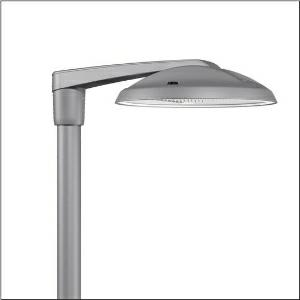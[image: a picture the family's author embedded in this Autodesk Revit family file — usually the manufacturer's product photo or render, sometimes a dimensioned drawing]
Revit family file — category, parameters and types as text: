
# Revit family: dl_r__50_iq_mini___st1_0a_5xa248d31v08le_d4cd
name_source: partatom
category: Lighting Fixtures
units: mm (PartAtom-declared; Revit-internal decimal feet)

## family parameters
Cut with Voids When Loaded = No
Host = Face
Light Source = No
Part Type = Normal
Room Calculation Point = No
Round Connector Dimension = Use Diameter
Shared = No

## types (1)
- --- (1 x LED, 10390 lm, 66 W, 3000K)
    Apparent Load = 66 VA
    CIE Flux Codes = 37 72 97 100 100
    Color Rendering = 70
    Color Temperature = 3000K
    Default Elevation = 1800 mm
    Description = DL® 50 iQ mini, mast luminaire, primary light control with lens, of PMMA, primary optical cover: cover, of toughened safety glass, transparent, light distribution: ST1.0a, light emission: direct distribution, primary light characteristic: asymmetric, installation type: post-top, side-entry, LED, High Power LED, rated luminous flux: 10.390lm, luminous efficacy: 157lm/W, light colour: 730, colour temperature: 3000K, control gear: iQ-Street Remote, D4i with power reduction, control: optimised constant luminous flux control (CLO 2.0), Desk-Remote (wireless, voltage-free reading and setting of iQ features in the workshop via application-optimized NFC function/RFID function), Light-Fading, Smart-Wire, Night-Set, Lumen-Switch, Temp-Guard, Auto-Match, Street-Remote, pre-setting: logarithmic dimming characteristic, mains connection: 230..240V, AC, 50/60Hz, connection cable pre-assembled, cable length: 8,5m, start of lifetime: 66W, end of service life: 69W, reduction: 30W, luminaire housing, of diecast aluminium, powder-coated, Siteco® metallic grey (DB 702S), inclination adjustable: 0°, 5°, 10° (post-top) | 0°, -5°, -10°, -15° (side-entry), please order mast post-top element or mast side-entry element separately, diameter: 500mm, height: 115mm, post-top: for spigot size d x l = 76 x 100mm; with reducer (optional accessory) 60 x 100mm | side-entry: for spigot size d x l = 60 x 100mm; with reducer (optional accessory) 42 x 100mm, mounting height: 4..6m, Smart Interface above, protection rating (complete): IP66, insulation class (complete): insulation class II (safety insulation), certification: CE, ENEC, ENEC+, VDE, impact resistance: IK08, permissible operating ambient temperature for outdoor applications: -25..+40°C, standard-compliant lighting for roads and squares, packaging unit: 1 piece

Light Distribution: ST1.0a
    Height = 115 mm
    Lamp = 1 x LED
    Lamp Light Flux = 10390 lm
    Lamp Power = 66 W
    Lamp count = 1
    Length = 500 mm
    Luminous efficacy = 157 lm/W
    Manufacturer = Siteco
    ModVariant = No
    Model = 5XA248D31V08LE
    Number of Poles = 1
    OnlyDefault = Yes
    Power Factor = 1
    Product Name = DL® 50 iQ mini | ST1.0a
    Product group = mast luminaire | pylon top
    ProductGroupID = 6100
    Protection Class = Protection class II
    Protection Degree = IP 66
    RLX_Detail_Level = 1
    RLX_Emergency_Light_Flux = 0 lm
    RLX_Emergency_Type = 0
    RLX_Emergency_Type_DB = No
    RlxData = <blob elided: 106745 chars, md5=d9678d95>
    Socket = socket
    Standby Power = 0 W
    System Light Flux = 10390 lm
    System Power = 66 W
    Type Comments = factory setting: luminous flux: 100 % | dim-lin: 254 | 691 mA
    Type Image = l_1251788.jpg
    URL = http://relux.com
    VarID = @adj_088875
    Voltage = 0 V
    Weight = 0.00 kg
    Width = 0 mm  [stored 0 ft]

note: [stored X ft] marks values corroborated as IEEE doubles in the binary element streams (Revit-internal decimal feet)

## geometry (parser evidence)
native form markers: Blend x4, Sweep x9
no freeform markers — native parametric forms only
